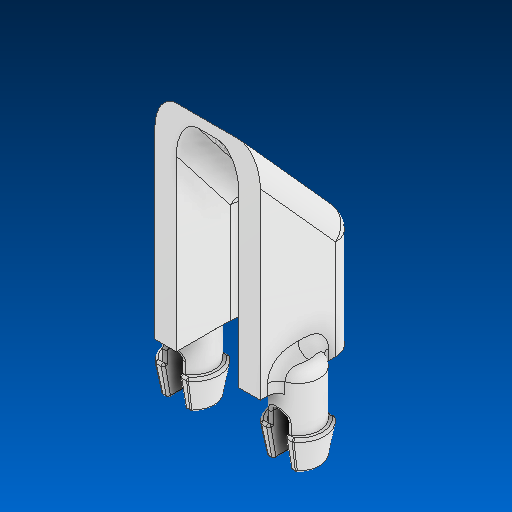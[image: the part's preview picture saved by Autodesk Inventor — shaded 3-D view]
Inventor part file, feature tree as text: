
AUTODESK INVENTOR PART (.ipt)
format: ipt  version: 2022.2 (Build 262287000, 287)  size: 370,176 bytes
history: native  units: in
note: dims shown in document units (in); Inventor stores cm internally (conversion verified against a paired STEP export)
features: fillet x1
ambient origin geometry x8: Origin, YZ Plane, XZ Plane, XY Plane, X Axis, Y Axis, Z Axis, Center Point
bodies: Solid1 (feature_tree)
feature tree (1):
  fillet  "Fillet3"  [1 undecoded]
note: 1 required parameter value undecoded (feature->parameter linkage not recoverable at this tier; creation-order binding heuristic only, values carry confidence <= 0.55)
